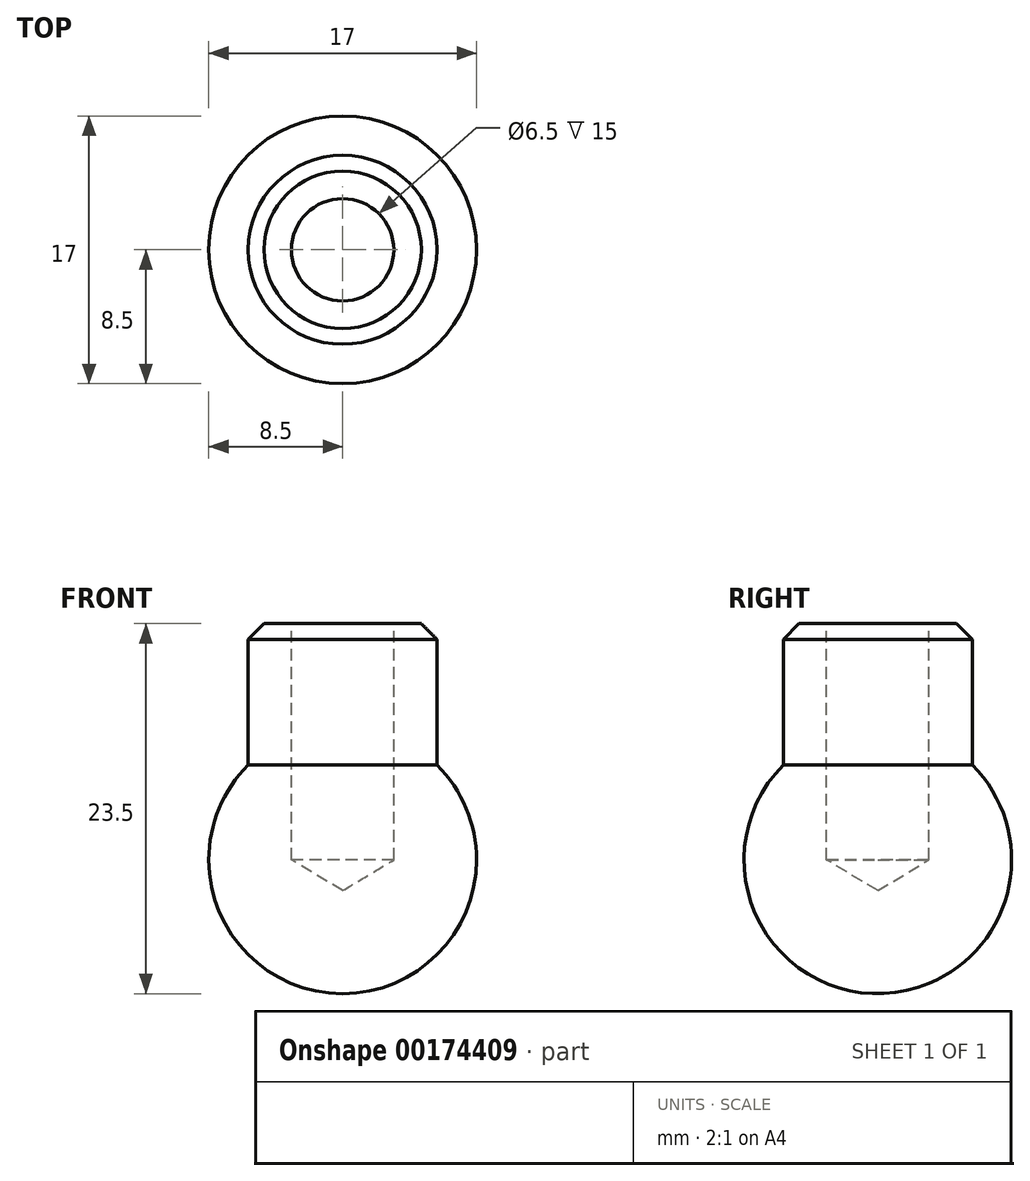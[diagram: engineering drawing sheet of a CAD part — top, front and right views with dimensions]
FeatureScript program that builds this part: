
annotation { "Feature Type Name" : "Feature", "Feature Type Description" : "" }
export const myFeature = defineFeature(function(context is Context, id is Id, definition is map)
    precondition{}
    {
        {
            var Q0;
            Q0=qCreatedBy(makeId("Top.planeOp"),FACE);
            var sketch = newSketch(context, id + "F0", { "sketchPlane" : qUnion([Q0])});
            skCircle(sketch, "E0", {"center": v(0, 0) * mm, "radius": 6 * mm});
            skSolve(sketch);
        }
        {
            var Q0;
            Q0=makeQuery(id+"F0.imprint","IMPRINT",FACE,{"disambiguationData":[TD([[makeQuery(id+"F0.imprint","IMPRINT",EDGE,{"derivedFrom":sQuery(id+"F0.wireOp",EDGE,"E0")}),1.0]])]});
            extrude(context, id + "F1", {"entities" : qUnion([Q0]), "depth" : 15 * mm});
        }
        {
            var Q0;
            Q0=qCreatedBy(makeId("Top.planeOp"),FACE);
            var sketch = newSketch(context, id + "F2", { "sketchPlane" : qUnion([Q0])});
            skArc(sketch, "E1", {"start": v(8.5, 0) * mm, "mid": v(0, 8.5) * mm, "end": v(-8.5, 0) * mm});
            skLineSegment(sketch, "E2", {"start": v(-8.5, 0) * mm, "end": v(8.5, 0) * mm});
            skSolve(sketch);
        }
        {
            var Q0;
            Q0=makeQuery(id+"F2.imprint","IMPRINT",FACE,{"disambiguationData":[TD([[makeQuery(id+"F2.imprint","IMPRINT",EDGE,{"derivedFrom":sQuery(id+"F2.wireOp",EDGE,"E1")}),1.0]])]});
            var Q1;
            Q1=sQuery(id+"F2.wireOp",EDGE,"E1");
            var Q2;
            Q2=sQuery(id+"F2.wireOp",EDGE,"E2");
            revolve(context, id + "F3", {"operationType" : NewBodyOperationType.ADD, "entities" : qUnion([Q0]), "surfaceEntities" : qUnion([Q1]), "axis" : qUnion([Q2]), "revolveType" : RevolveType.FULL});
        }
        {
            var Q0;
            Q0=makeQuery(id+"F1.opExtrude","CAP_FACE",FACE,{"disambiguationData":[OSD([sQuery(id+"F0.wireOp",EDGE,"E0")])],"isStart":false});
            var sketch = newSketch(context, id + "F4", { "sketchPlane" : qUnion([Q0])});
            skCircle(sketch, "E3.0", {"center": v(0, 0) * mm, "radius": 6 * mm});
            skSolve(sketch);
        }
        {
            var Q0;
            Q0=sQuery(id+"F4.wireOp",VERTEX,"E3.0.center");
            var Q1;
            Q1=makeQuery(id+"F1.opExtrude","SWEPT_BODY",BODY,{"disambiguationData":[OSD([sQuery(id+"F0.wireOp",EDGE,"E0")])]});
            hole(context, id + "F5", {"style" : HoleStyle.SIMPLE, "endStyle" : HoleEndStyle.BLIND, "holeDiameter" : 6.5 * mm, "holeDepth" : 15 * mm, "startFromSketch" : true, "locations" : qUnion([Q0]), "scope" : qUnion([Q1])});
        }
        {
            var Q0;
            Q0=makeQuery(id+"F1.opExtrude","CAP_EDGE",EDGE,{"disambiguationData":[OSD([sQuery(id+"F0.wireOp",EDGE,"E0")])],"isStart":false});
            chamfer(context, id + "F6", {"entities" : qUnion([Q0]), "width" : 1 * mm, "tangentPropagation" : true});
        }
    });
